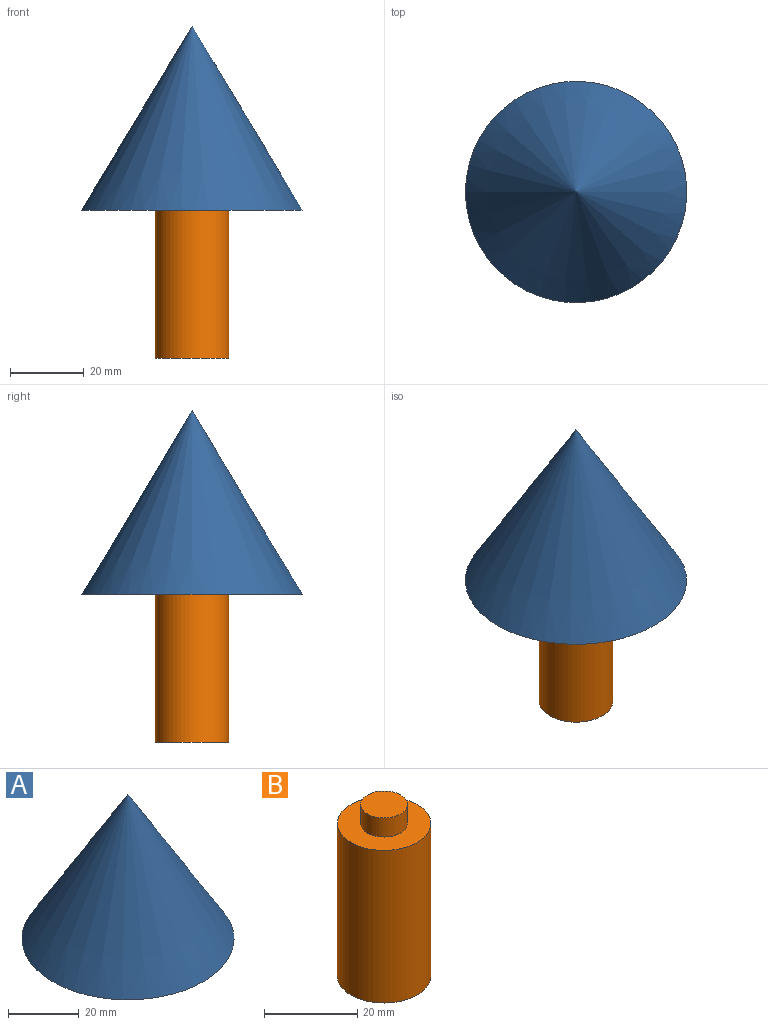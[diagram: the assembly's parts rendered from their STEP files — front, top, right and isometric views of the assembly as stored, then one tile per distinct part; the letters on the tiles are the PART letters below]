
ASSEMBLY  parts=2 mates=1
PART A: 4 faces, bbox 60x60x50 mm
  f0: plane 60x60mm, normal (0,0,-1), area 2748.9mm2, adj f1,f2
  f1: cone r=0mm half-angle=31deg, axis (0,0,-1), area 5495.5mm2, adj f0
  f2: cylinder r=5mm len=10mm, axis (0,0,-1), area 157.1mm2, adj f0,f3
  f3: plane 10x10mm, normal (0,0,-1), area 78.5mm2, adj f2
PART B: 5 faces, bbox 20x20x45 mm
  f0: cylinder r=10mm len=40mm, axis (0,0,-1), area 2513.3mm2, adj f1,f2
  f1: plane 20x20mm, normal (0,0,1), area 235.6mm2, adj f0,f3
  f2: plane 20x20mm, normal (0,0,-1), area 314.2mm2, adj f0
  f3: cylinder r=5mm len=10mm, axis (0,0,-1), area 157.1mm2, adj f1,f4
  f4: plane 10x10mm, normal (0,0,1), area 78.5mm2, adj f3
PLACE A t=(-11.41,-38.74,71.14)mm
PLACE B t=(-11.41,-38.74,31.14)mm
MATE fastened B.f0 <-> A.f1  axis (0,0,1) through (-11.41,-38.74,71.14)mm
